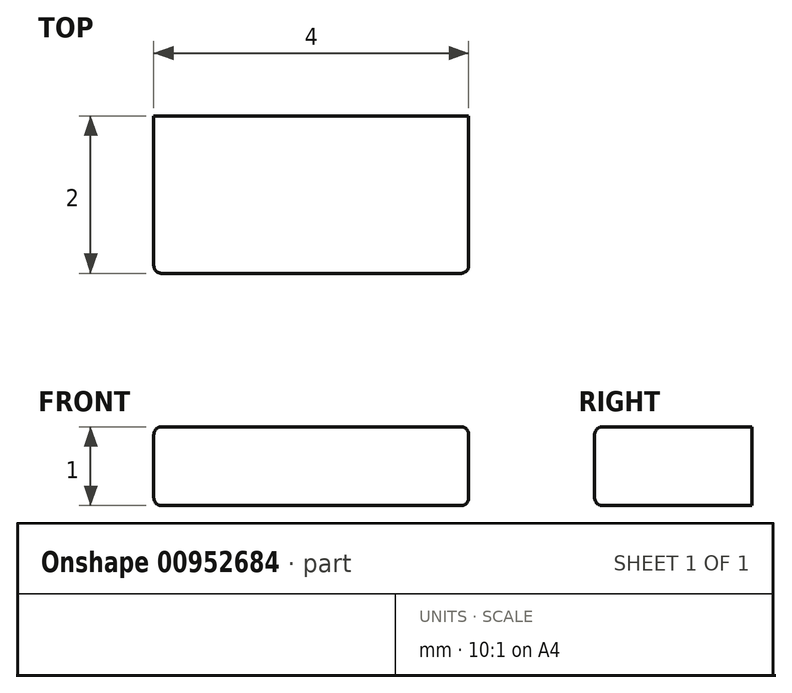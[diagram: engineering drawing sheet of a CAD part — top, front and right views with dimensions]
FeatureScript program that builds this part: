
annotation { "Feature Type Name" : "Feature", "Feature Type Description" : "" }
export const myFeature = defineFeature(function(context is Context, id is Id, definition is map)
    precondition{}
    {
        {
            var Q0;
            Q0=qCreatedBy(makeId("Front.planeOp"),FACE);
            var sketch = newSketch(context, id + "F0", { "sketchPlane" : qUnion([Q0])});
            skLineSegment(sketch, "E0.bottom", {"start": v(2, -0.5) * mm, "end": v(-2, -0.5) * mm});
            skLineSegment(sketch, "E0.top", {"start": v(2, 0.5) * mm, "end": v(-2, 0.5) * mm});
            skLineSegment(sketch, "E0.left", {"start": v(2, -0.5) * mm, "end": v(2, 0.5) * mm});
            skLineSegment(sketch, "E0.right", {"start": v(-2, -0.5) * mm, "end": v(-2, 0.5) * mm});
            skPoint(sketch, "E0.middle", {"position": v(0, 0) * mm});
            skSolve(sketch);
        }
        {
            var Q0;
            Q0=makeQuery(id+"F0.imprint","IMPRINT",FACE,{"disambiguationData":[TD([[makeQuery(id+"F0.imprint","IMPRINT",EDGE,{"derivedFrom":sQuery(id+"F0.wireOp",EDGE,"E0.bottom")}),-1.0]])]});
            extrude(context, id + "F1", {"entities" : qUnion([Q0]), "endBound" : BoundingType.SYMMETRIC, "depth" : 2 * mm, "offsetDistance" : 25 * mm});
        }
        {
            var Q0;
            Q0=makeQuery(id+"F1.opExtrude","CAP_EDGE",EDGE,{"disambiguationData":[OSD([sQuery(id+"F0.wireOp",EDGE,"E0.bottom")])],"isStart":false});
            var Q1;
            Q1=makeQuery(id+"F1.opExtrude","CAP_EDGE",EDGE,{"disambiguationData":[OSD([sQuery(id+"F0.wireOp",EDGE,"E0.top")])],"isStart":false});
            var Q2;
            Q2=makeQuery(id+"F1.opExtrude","CAP_EDGE",EDGE,{"disambiguationData":[OSD([sQuery(id+"F0.wireOp",EDGE,"E0.left")])],"isStart":false});
            var Q3;
            Q3=makeQuery(id+"F1.opExtrude","CAP_EDGE",EDGE,{"disambiguationData":[OSD([sQuery(id+"F0.wireOp",EDGE,"E0.right")])],"isStart":false});
            var Q4;
            Q4=makeQuery(id+"F1.opExtrude","SWEPT_EDGE",EDGE,{"disambiguationData":[OSD([sQuery(id+"F0.wireOp",EDGE,"E0.top"),sQuery(id+"F0.wireOp",EDGE,"E0.right")])]});
            var Q5;
            Q5=makeQuery(id+"F1.opExtrude","SWEPT_EDGE",EDGE,{"disambiguationData":[OSD([sQuery(id+"F0.wireOp",EDGE,"E0.top"),sQuery(id+"F0.wireOp",EDGE,"E0.left")])]});
            var Q6;
            Q6=makeQuery(id+"F1.opExtrude","SWEPT_EDGE",EDGE,{"disambiguationData":[OSD([sQuery(id+"F0.wireOp",EDGE,"E0.bottom"),sQuery(id+"F0.wireOp",EDGE,"E0.left")])]});
            var Q7;
            Q7=makeQuery(id+"F1.opExtrude","SWEPT_EDGE",EDGE,{"disambiguationData":[OSD([sQuery(id+"F0.wireOp",EDGE,"E0.bottom"),sQuery(id+"F0.wireOp",EDGE,"E0.right")])]});
            fillet(context, id + "F2", {"entities" : qUnion([Q0, Q1, Q2, Q3, Q4, Q5, Q6, Q7]), "radius" : 0.1 * mm, "tangentPropagation" : true, "allowEdgeOverflow" : false});
        }
    });
